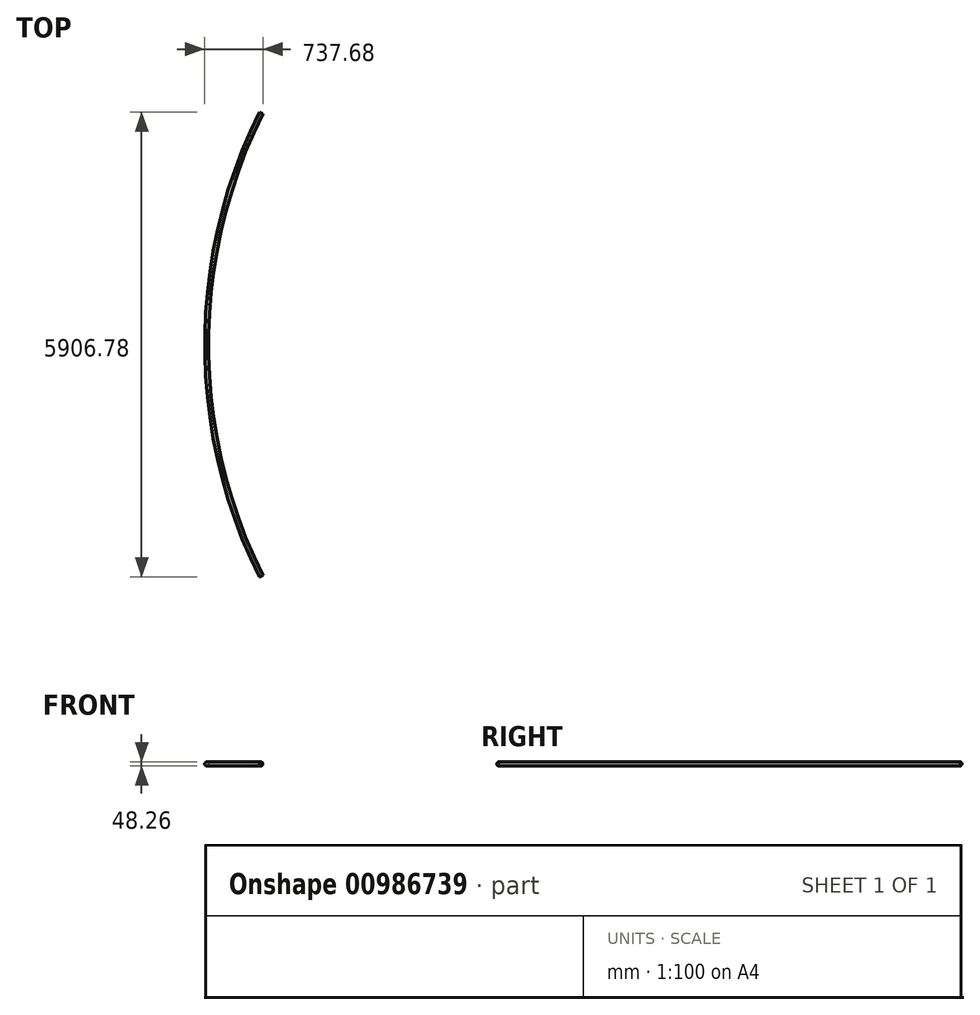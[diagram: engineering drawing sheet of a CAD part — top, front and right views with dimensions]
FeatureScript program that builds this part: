
annotation { "Feature Type Name" : "Feature", "Feature Type Description" : "" }
export const myFeature = defineFeature(function(context is Context, id is Id, definition is map)
    precondition{}
    {
        {
            var Q0;
            Q0=qCreatedBy(makeId("Front.planeOp"),FACE);
            var sketch = newSketch(context, id + "F0", { "sketchPlane" : qUnion([Q0])});
            skCircle(sketch, "E0", {"center": v(0, 0) * mm, "radius": 24.13 * mm});
            skLineSegment(sketch, "E1", {"start": v(0, 0) * mm, "end": v(6603, 0) * mm, "construction": true});
            skLineSegment(sketch, "E2", {"start": v(6603, 0) * mm, "end": v(6603, -100) * mm, "construction": true});
            skCircle(sketch, "E3.0", {"center": v(0, 0) * mm, "radius": 21.36 * mm});
            skSolve(sketch);
        }
        {
            var Q0;
            Q0=makeQuery(id+"F0.imprint","IMPRINT",FACE,{"disambiguationData":[TD([[makeQuery(id+"F0.imprint","IMPRINT",EDGE,{"derivedFrom":sQuery(id+"F0.wireOp",EDGE,"E0")}),1.0]])]});
            var Q1;
            Q1=sQuery(id+"F0.wireOp",EDGE,"E2");
            revolve(context, id + "F1", {"surfaceOperationType" : NewSurfaceOperationType.NEW, "entities" : qUnion([Q0]), "axis" : qUnion([Q1]), "revolveType" : RevolveType.SYMMETRIC, "angle" : 52.93 * degree});
        }
    });
